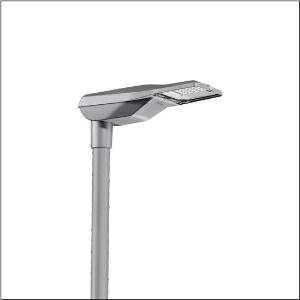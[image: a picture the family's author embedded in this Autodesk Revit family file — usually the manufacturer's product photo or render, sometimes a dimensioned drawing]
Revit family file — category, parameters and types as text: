
# Revit family: streetlight_sl_21_iq_micro___stw1_0a_5xe1e21d08cb_e74e
name_source: partatom
category: Lighting Fixtures
units: mm (PartAtom-declared; Revit-internal decimal feet)

## family parameters
Cut with Voids When Loaded = No
Host = Face
Light Source = No
Part Type = Normal
Room Calculation Point = No
Round Connector Dimension = Use Diameter
Shared = No

## types (1)
- --- (1 x LED, 2380 lm, 19.4 W, 2200K)
    Apparent Load = 19 VA
    CIE Flux Codes = 38 75 98 100 100
    Color Rendering = 70
    Color Temperature = 2200K
    Default Elevation = 1800 mm
    Description = Streetlight SL 21 iQ micro, mast luminaire, primary light control with lens, of PMMA, primary optical cover: cover, of toughened safety glass, transparent, light distribution: STW1.0a, light emission: direct distribution, primary light characteristic: asymmetric, installation type: post-top, side-entry, LED, High Power LED, rated luminous flux: 2.380lm, luminous efficacy: 123lm/W, light colour: 722, colour temperature: 2200K, control gear: iQ-Comfort, control: Auto-Match, Temp-Guard, Lumen-Switch, Night-Set, Smart-Wire, Light-Fading, Desk-Remote (wireless, voltage-free reading and setting of iQ features in the workshop via application-optimized NFC function/RFID function), optimised constant luminous flux control (CLO 2.0), pre-setting: linear dimming characteristic, mains connection: 220..240V, AC, 50/60Hz, start of lifetime: 19W, end of service life: 20W, reduction: 10W, luminaire housing, of diecast aluminium, powder-coated, Siteco® metallic grey (DB 702S), corrosivity category C5 high according to DIN EN ISO 12944, please order mast flange separately, inclination adjustable: 0°, 5°, 10°, 15°, sealing non-destructively replaceable, multi-level sealing system, length: 528mm, width: 235mm, height: 110mm, mast flange for spigot size: 42mm (side-entry): 5XC10008XM4, 60/48mm (side-entry/post-top): 5XC10108XM2, 76/60mm (side-entry/post-top): 5XC10108XM1, protection rating (complete): IP66, insulation class (complete): insulation class II (safety insulation), certification: CE, ENEC, ENEC+, VDE, impact resistance: IK10, permissible operating ambient temperature for outdoor applications: -40..+50°C, standard-compliant lighting for roads and squares, packaging unit: 1 piece

Light Distribution: STW1.0a
    Height = 110 mm
    Lamp = 1 x LED
    Lamp Light Flux = 2380 lm
    Lamp Power = 19.4 W
    Lamp count = 1
    Length = 528 mm
    Luminous efficacy = 123 lm/W
    Manufacturer = Siteco
    ModVariant = No
    Model = 5XE1E21D08CB
    Number of Poles = 1
    OnlyDefault = Yes
    Power Factor = 1
    Product Name = Streetlight SL 21 iQ micro | STW1.0a
    Product group = mast luminaire | pylon top
    ProductGroupID = 6100
    Protection Class = Protection class II
    Protection Degree = IP 66
    RLX_Detail_Level = 1
    RLX_Emergency_Light_Flux = 0 lm
    RLX_Emergency_Type = 0
    RLX_Emergency_Type_DB = No
    RlxData = <blob elided: 98833 chars, md5=68e1a195>
    Socket = socket
    Standby Power = 0 W
    System Light Flux = 2380 lm
    System Power = 19 W
    Type Comments = factory setting: luminous flux: 100 % | dim-lin: 254 | 387 mA
    Type Image = l_1006881.jpg
    URL = http://relux.com
    VarID = @adj_142245
    Voltage = 0 V
    Weight = 0.00 kg
    Width = 235 mm

## geometry (parser evidence)
native form markers: Blend x4, Sweep x11
no freeform markers — native parametric forms only
